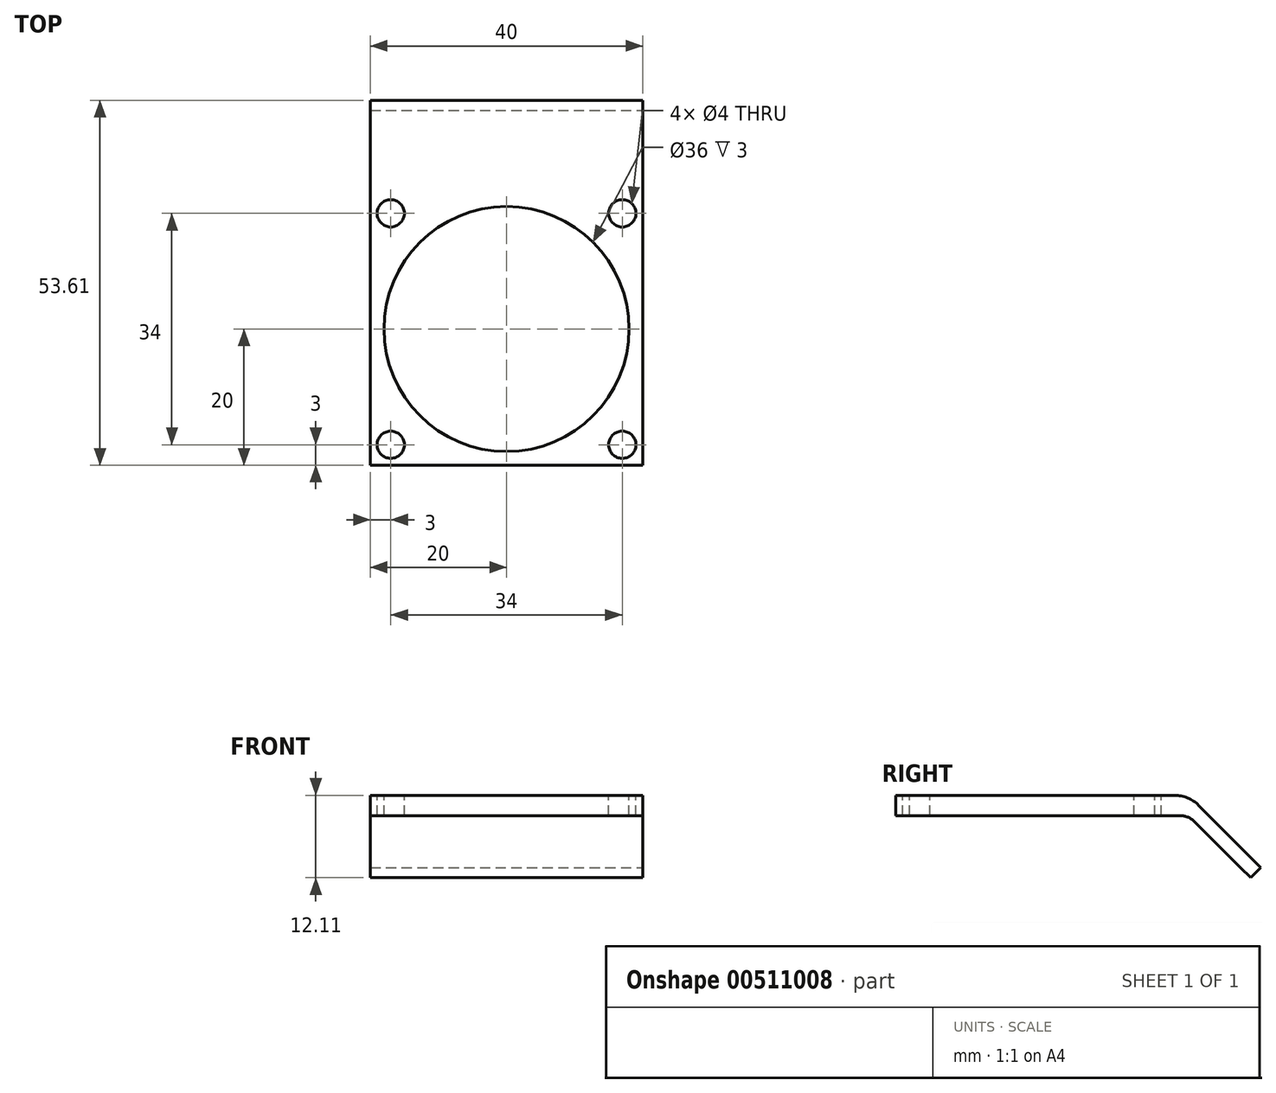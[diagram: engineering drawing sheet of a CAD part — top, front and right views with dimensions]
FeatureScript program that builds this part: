
annotation { "Feature Type Name" : "Feature", "Feature Type Description" : "" }
export const myFeature = defineFeature(function(context is Context, id is Id, definition is map)
    precondition{}
    {
        {
            var Q0;
            Q0=qCreatedBy(makeId("Top.planeOp"),FACE);
            var sketch = newSketch(context, id + "F0", { "sketchPlane" : qUnion([Q0])});
            skLineSegment(sketch, "E0.bottom", {"start": v(0, 0) * mm, "end": v(40, 0) * mm});
            skLineSegment(sketch, "E0.top", {"start": v(0, 40) * mm, "end": v(40, 40) * mm});
            skLineSegment(sketch, "E0.left", {"start": v(0, 0) * mm, "end": v(0, 40) * mm});
            skLineSegment(sketch, "E0.right", {"start": v(40, 0) * mm, "end": v(40, 40) * mm});
            skSolve(sketch);
        }
        {
            var Q0;
            Q0=makeQuery(id+"F0.imprint","IMPRINT",FACE,{"disambiguationData":[TD([[makeQuery(id+"F0.imprint","IMPRINT",EDGE,{"derivedFrom":sQuery(id+"F0.wireOp",EDGE,"E0.bottom")}),1.0]])]});
            extrude(context, id + "F1", {"entities" : qUnion([Q0]), "depth" : 3 * mm});
        }
        {
            var Q0;
            Q0=makeQuery(id+"F1.opExtrude","CAP_FACE",FACE,{"disambiguationData":[OSD([sQuery(id+"F0.wireOp",EDGE,"E0.bottom"),sQuery(id+"F0.wireOp",EDGE,"E0.top"),sQuery(id+"F0.wireOp",EDGE,"E0.left"),sQuery(id+"F0.wireOp",EDGE,"E0.right")])],"isStart":false});
            var sketch = newSketch(context, id + "F2", { "sketchPlane" : qUnion([Q0])});
            skCircle(sketch, "E1", {"center": v(20, 20) * mm, "radius": 18 * mm});
            skSolve(sketch);
        }
        {
            var Q0;
            Q0 = qSketchRegion(id + "F2", true);
            extrude(context, id + "F3", {"entities" : qUnion([Q0]), "operationType" : NewBodyOperationType.REMOVE, "endBound" : BoundingType.THROUGH_ALL, "oppositeDirection" : true, "depth" : 25 * mm});
        }
        {
            var Q0;
            Q0=makeQuery(id+"F1.opExtrude","CAP_FACE",FACE,{"disambiguationData":[OSD([sQuery(id+"F0.wireOp",EDGE,"E0.bottom"),sQuery(id+"F0.wireOp",EDGE,"E0.top"),sQuery(id+"F0.wireOp",EDGE,"E0.left"),sQuery(id+"F0.wireOp",EDGE,"E0.right")])],"isStart":false});
            var sketch = newSketch(context, id + "F4", { "sketchPlane" : qUnion([Q0])});
            skCircle(sketch, "E2", {"center": v(3, 37) * mm, "radius": 2 * mm});
            skCircle(sketch, "E3", {"center": v(3, 3) * mm, "radius": 2 * mm});
            skCircle(sketch, "E4", {"center": v(37, 37) * mm, "radius": 2 * mm});
            skCircle(sketch, "E5", {"center": v(37, 3) * mm, "radius": 2 * mm});
            skSolve(sketch);
        }
        {
            var Q0;
            Q0 = qSketchRegion(id + "F4", true);
            extrude(context, id + "F5", {"entities" : qUnion([Q0]), "operationType" : NewBodyOperationType.REMOVE, "endBound" : BoundingType.THROUGH_ALL, "oppositeDirection" : true, "depth" : 25 * mm});
        }
        {
            var Q0;
            Q0=makeQuery(id+"F1.opExtrude","SWEPT_FACE",FACE,{"disambiguationData":[OSD([sQuery(id+"F0.wireOp",EDGE,"E0.right")])]});
            var sketch = newSketch(context, id + "F6", { "sketchPlane" : qUnion([Q0])});
            skLineSegment(sketch, "E6.bottom", {"start": v(40, 3) * mm, "end": v(43, 3) * mm});
            skLineSegment(sketch, "E6.top", {"start": v(50.6, -7.6) * mm, "end": v(53.6, -7.6) * mm});
            skLineSegment(sketch, "E6.left", {"start": v(40, 3) * mm, "end": v(50.6, -7.6) * mm});
            skLineSegment(sketch, "E6.right", {"start": v(43, 3) * mm, "end": v(53.6, -7.6) * mm});
            skPoint(sketch, "E7", {"position": v(43, 0) * mm});
            skPoint(sketch, "E8", {"position": v(42.4, -1.18) * mm});
            skPoint(sketch, "E9", {"position": v(41.5, 1.5) * mm});
            skPoint(sketch, "E9.positionSnap0", {"position": v(41.5, 3) * mm});
            skLineSegment(sketch, "E10", {"start": v(43, 0) * mm, "end": v(40, 0) * mm});
            skLineSegment(sketch, "E11", {"start": v(40, 0) * mm, "end": v(40, 3) * mm});
            skLineSegment(sketch, "E12", {"start": v(53.6, -7.6) * mm, "end": v(52.1, -9.1) * mm});
            skLineSegment(sketch, "E13", {"start": v(52.1, -9.1) * mm, "end": v(50.6, -7.6) * mm});
            skSolve(sketch);
        }
        {
            var Q0;
            Q0 = qSketchRegion(id + "F6", true);
            extrude(context, id + "F7", {"entities" : qUnion([Q0]), "operationType" : NewBodyOperationType.ADD, "oppositeDirection" : true, "depth" : 40 * mm});
        }
        {
            var Q0;
            Q0=makeQuery(id+"F7.opExtrude","SWEPT_EDGE",EDGE,{"disambiguationData":[OSD([sQuery(id+"F6.wireOp",EDGE,"E6.bottom"),sQuery(id+"F6.wireOp",EDGE,"E6.right")])]});
            fillet(context, id + "F8", {"entities" : qUnion([Q0]), "radius" : 5 * mm, "tangentPropagation" : true, "allowEdgeOverflow" : false});
        }
        {
            var Q0;
            Q0=makeQuery(id+"F7.opExtrude","SWEPT_FACE",FACE,{"disambiguationData":[OSD([sQuery(id+"F6.wireOp",EDGE,"E6.right")])]});
            var sketch = newSketch(context, id + "F9", { "sketchPlane" : qUnion([Q0])});
            skCircle(sketch, "E14", {"center": v(30, 36.79) * mm, "radius": 2.5 * mm});
            skCircle(sketch, "E15", {"center": v(10, 36.79) * mm, "radius": 2.5 * mm});
            skPoint(sketch, "E15.centerSnap0", {"position": v(0, 36.79) * mm});
            skSolve(sketch);
        }
        {
            var Q0;
            Q0 = qSketchRegion(id + "F9", true);
            extrude(context, id + "F10", {"entities" : qUnion([Q0]), "operationType" : NewBodyOperationType.REMOVE, "endBound" : BoundingType.THROUGH_ALL, "oppositeDirection" : true, "depth" : 25 * mm});
        }
        {
            var Q0;
            Q0=makeQuery(id+"F7.opExtrude","SWEPT_EDGE",EDGE,{"disambiguationData":[OSD([sQuery(id+"F6.wireOp",EDGE,"E6.left"),sQuery(id+"F6.wireOp",EDGE,"E10")])]});
            fillet(context, id + "F11", {"entities" : qUnion([Q0]), "radius" : 3 * mm, "tangentPropagation" : true, "allowEdgeOverflow" : false});
        }
    });
